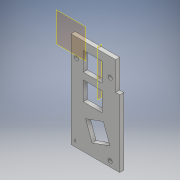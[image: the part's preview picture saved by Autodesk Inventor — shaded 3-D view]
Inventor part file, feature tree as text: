
AUTODESK INVENTOR PART (.ipt)
format: ipt  version: 2017 (Build 210142000, 142)  size: 143,872 bytes
history: native  units: mm
features: other x3, plane x2, extrude x1, mirror x1, sketch x1
ambient origin geometry x8: Origin, YZ Plane, XZ Plane, XY Plane, X Axis, Y Axis, Z Axis, Center Point
bodies: Solid1 (feature_tree)
feature tree (8):
  other  "k2_t2_l1.ipt"
  extrude  "Extrusion1"  Depth=50.0mm
  plane  "Work Plane2"
  mirror  "Mirror1"
  other  "Solid3::k2_t2_l1.ipt"
  other  "TaggingFeature1"
  plane  "Work Plane1"
  sketch  "Sketch2"  dims[d0=10.0mm d1=50.0mm d2=3.0mm d3=0.0mm d4=-13.5mm]
